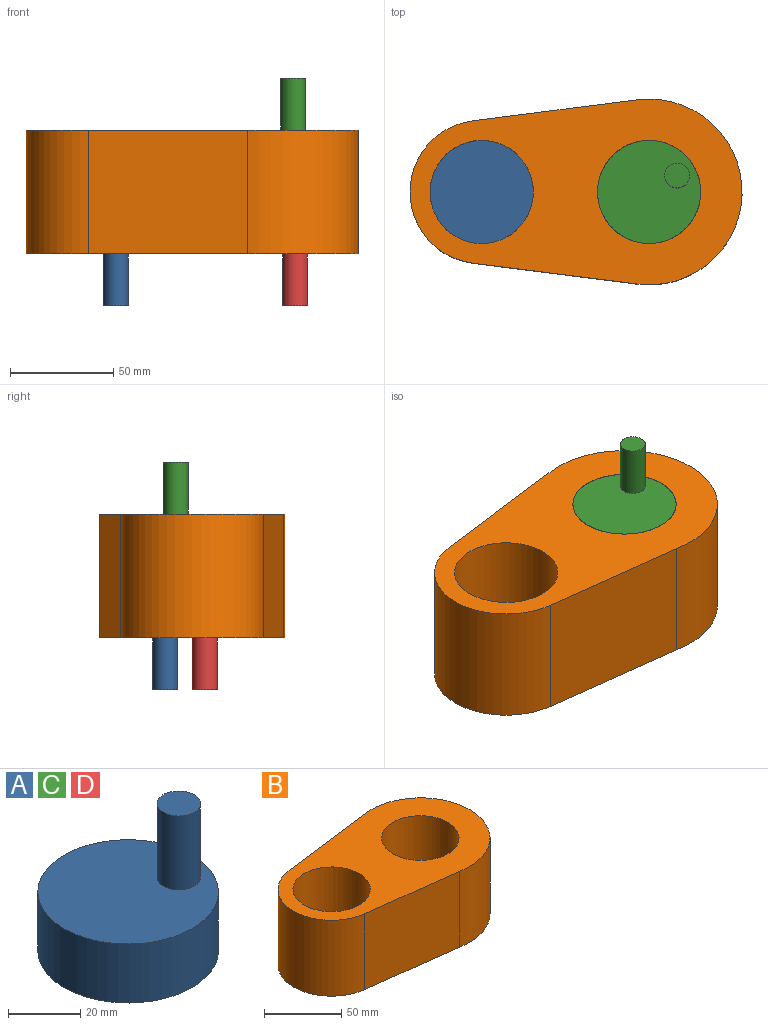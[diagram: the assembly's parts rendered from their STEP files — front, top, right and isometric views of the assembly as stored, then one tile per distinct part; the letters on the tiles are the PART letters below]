
ASSEMBLY  parts=4 mates=3
PART A: 5 faces, bbox 50x50x45 mm
  f0: cylinder r=25mm len=50mm, axis (0,0,-1), area 3141.6mm2, adj f1,f2
  f1: plane 50x50mm, normal (0,0,1), area 1850mm2, adj f0,f3
  f2: plane 50x50mm, normal (0,0,-1), area 1963.5mm2, adj f0
  f3: cylinder r=6.01mm len=25mm, axis (0,0,-1), area 944.1mm2, adj f1,f4
  f4: plane 12.02x12.02mm, normal (0,0,1), area 113.5mm2, adj f3
PART B: 8 faces, bbox 160.8x90x60 mm
  f0: cylinder r=45mm len=90mm, axis (0,0,-1), area 9333.4mm2, adj f1,f3,f6,f7
  f1: plane 79.75x60mm, normal (-0.13,0.99,0), area 4823.9mm2, adj f0,f2,f6,f7
  f2: cylinder r=34.73mm len=68.9mm, axis (0,0,-1), area 6018.5mm2, adj f1,f3,f6,f7
  f3: plane 77x60mm, normal (-0.13,-0.99,0), area 4657mm2, adj f0,f2,f6,f7
  f4: cylinder r=25mm len=60mm, axis (0,0,-1), area 9424.8mm2, adj f6,f7
  f5: cylinder r=25mm len=60mm, axis (0,0,-1), area 9424.8mm2, adj f6,f7
  f6: plane 160.78x90mm, normal (0,0,1), area 7658.9mm2, adj f0,f1,f2,f3,f4,f5
  f7: plane 160.78x90mm, normal (0,0,-1), area 7658.9mm2, adj f0,f1,f2,f3,f4,f5
PART C: same geometry as A
PART D: same geometry as A
PLACE A rot(axis=(0.95,0.32,0),180deg) t=(-100.18,-30.4,-5.99)mm
PLACE B t=(-19.12,-30.4,4.01)mm fixed
PLACE C rot(axis=(0,0,1),48.7deg) t=(-19.12,-30.4,14.01)mm
PLACE D rot(axis=(0.94,-0.35,0),180deg) t=(-19.12,-30.4,-5.99)mm
MATE revolute C.f0 <-> B.f0  axis (0,0,1) through (-19.12,-30.4,34.01)mm
MATE revolute D.f0 <-> B.f0  axis (0,0,1) through (-19.12,-30.4,-25.99)mm
MATE revolute A.f0 <-> B.f2  axis (0,0,-1) through (-100.18,-30.4,-25.99)mm
